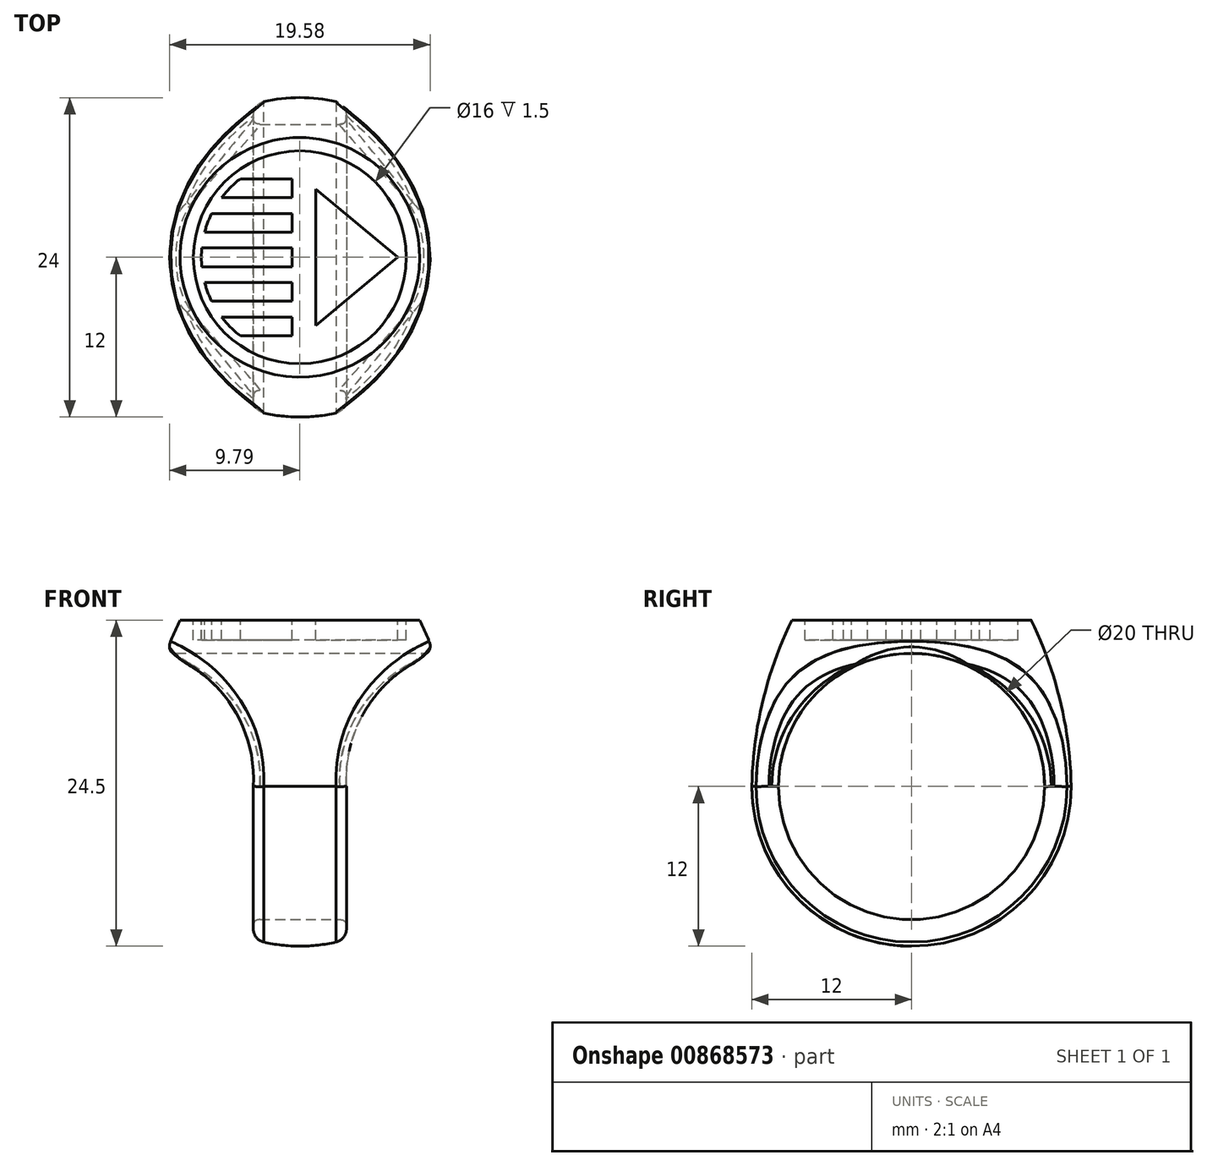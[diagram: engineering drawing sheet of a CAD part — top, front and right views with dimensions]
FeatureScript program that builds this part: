
annotation { "Feature Type Name" : "Feature", "Feature Type Description" : "" }
export const myFeature = defineFeature(function(context is Context, id is Id, definition is map)
    precondition{}
    {
        {
            var Q0;
            Q0=qCreatedBy(makeId("Right.planeOp"),FACE);
            var sketch = newSketch(context, id + "F0", { "sketchPlane" : qUnion([Q0])});
            skLineSegment(sketch, "E0", {"start": v(0, 0) * mm, "end": v(0, -24.5) * mm});
            skLineSegment(sketch, "E1", {"start": v(0, 0) * mm, "end": v(-9, 0) * mm});
            skArc(sketch, "E2", {"start": v(-12, -12.5) * mm, "mid": v(-8.49, -20.99) * mm, "end": v(0, -24.5) * mm});
            skLineSegment(sketch, "E3", {"start": v(0, -12.5) * mm, "end": v(-12, -12.5) * mm, "construction": true});
            skArc(sketch, "E4", {"start": v(-9, 0) * mm, "mid": v(-11.18, -6.09) * mm, "end": v(-12, -12.5) * mm});
            skSolve(sketch);
        }
        {
            var Q0;
            Q0=makeQuery(id+"F0.imprint","IMPRINT",FACE,{"disambiguationData":[TD([[makeQuery(id+"F0.imprint","IMPRINT",EDGE,{"derivedFrom":sQuery(id+"F0.wireOp",EDGE,"E0")}),-1.0]])]});
            var Q1;
            Q1=sQuery(id+"F0.wireOp",EDGE,"E0");
            revolve(context, id + "F1", {"entities" : qUnion([Q0]), "axis" : qUnion([Q1]), "revolveType" : RevolveType.FULL});
        }
        {
            var Q0;
            Q0=qCreatedBy(makeId("Right.planeOp"),FACE);
            var sketch = newSketch(context, id + "F2", { "sketchPlane" : qUnion([Q0])});
            skCircle(sketch, "E5", {"center": v(0, -12.5) * mm, "radius": 10 * mm});
            skSolve(sketch);
        }
        {
            var Q0;
            Q0=qSketchRegion(id+"F2",true);
            extrude(context, id + "F3", {"entities" : qUnion([Q0]), "operationType" : NewBodyOperationType.REMOVE, "endBound" : BoundingType.SYMMETRIC, "oppositeDirection" : true, "depth" : 25 * mm, "offsetDistance" : 25 * mm});
        }
        {
            var Q0;
            Q0=qCreatedBy(makeId("Front.planeOp"),FACE);
            var sketch = newSketch(context, id + "F4", { "sketchPlane" : qUnion([Q0])});
            skLineSegment(sketch, "E6", {"start": v(3.5, -26.5) * mm, "end": v(3.5, -12.5) * mm});
            skArc(sketch, "E7", {"start": v(10.15, -2.5) * mm, "mid": v(5.16, -6.39) * mm, "end": v(3.5, -12.5) * mm});
            skLineSegment(sketch, "E8", {"start": v(10.15, -2.5) * mm, "end": v(11.65, -2.5) * mm});
            skLineSegment(sketch, "E9", {"start": v(11.65, -2.5) * mm, "end": v(11.65, -26.5) * mm});
            skLineSegment(sketch, "E10", {"start": v(11.65, -26.5) * mm, "end": v(3.5, -26.5) * mm});
            skPoint(sketch, "E11.start.orphan", {"position": v(0, -24.5) * mm});
            skLineSegment(sketch, "E12", {"start": v(0, 0) * mm, "end": v(0, -24.5) * mm, "construction": true});
            skLineSegment(sketch, "E13.MirrorCS", {"start": v(-3.5, -26.5) * mm, "end": v(-3.5, -12.5) * mm});
            skArc(sketch, "E14.MirrorCS", {"start": v(-10.15, -2.5) * mm, "mid": v(-5.16, -6.39) * mm, "end": v(-3.5, -12.5) * mm});
            skLineSegment(sketch, "E15.MirrorCS", {"start": v(-11.65, -2.5) * mm, "end": v(-11.65, -26.5) * mm});
            skLineSegment(sketch, "E16.MirrorCS", {"start": v(-11.65, -26.5) * mm, "end": v(-3.5, -26.5) * mm});
            skLineSegment(sketch, "E17.MirrorCS", {"start": v(-10.15, -2.5) * mm, "end": v(-11.65, -2.5) * mm});
            skSolve(sketch);
        }
        {
            var Q0;
            Q0=qSketchRegion(id+"F4",true);
            extrude(context, id + "F5", {"entities" : qUnion([Q0]), "operationType" : NewBodyOperationType.REMOVE, "endBound" : BoundingType.SYMMETRIC, "depth" : 25 * mm, "offsetDistance" : 25 * mm});
        }
        {
            var Q0;
            Q0=makeQuery(id+"F1.opRevolve","SWEPT_FACE",FACE,{"disambiguationData":[OSD([sQuery(id+"F0.wireOp",EDGE,"E1")])]});
            var sketch = newSketch(context, id + "F6", { "sketchPlane" : qUnion([Q0])});
            skCircle(sketch, "E18", {"center": v(0, 0) * mm, "radius": 8 * mm});
            skLineSegment(sketch, "E19", {"start": v(-8, 0) * mm, "end": v(8, 0) * mm, "construction": true});
            skLineSegment(sketch, "E20", {"start": v(0, 7.69) * mm, "end": v(7.93, 1.07) * mm});
            skLineSegment(sketch, "E21", {"start": v(1.2, 0) * mm, "end": v(1.2, 5.13) * mm});
            skLineSegment(sketch, "E22", {"start": v(1.2, 5.13) * mm, "end": v(7.34, 0) * mm});
            skLineSegment(sketch, "E23", {"start": v(0, 7.69) * mm, "end": v(0, 0) * mm});
            skArc(sketch, "E24.trimOffspring", {"start": v(-4.47, 5.9) * mm, "mid": v(-5.22, 5.25) * mm, "end": v(-5.88, 4.5) * mm});
            skLineSegment(sketch, "E25", {"start": v(-7.37, 0.7) * mm, "end": v(-0.6, 0.7) * mm});
            skLineSegment(sketch, "E26", {"start": v(-0.6, 0.7) * mm, "end": v(-0.6, 0) * mm});
            skLineSegment(sketch, "E27", {"start": v(-7.15, 1.9) * mm, "end": v(-0.6, 1.9) * mm});
            skLineSegment(sketch, "E28", {"start": v(-0.6, 1.9) * mm, "end": v(-0.6, 3.3) * mm});
            skLineSegment(sketch, "E29", {"start": v(-0.6, 3.3) * mm, "end": v(-6.62, 3.3) * mm});
            skLineSegment(sketch, "E30", {"start": v(-5.88, 4.5) * mm, "end": v(-0.6, 4.5) * mm});
            skLineSegment(sketch, "E31", {"start": v(-0.6, 4.5) * mm, "end": v(-0.6, 5.9) * mm});
            skLineSegment(sketch, "E32", {"start": v(-0.6, 5.9) * mm, "end": v(-4.47, 5.9) * mm});
            skArc(sketch, "E33.trimOffspring", {"start": v(-7.37, 0.7) * mm, "mid": v(-7.4, 0.35) * mm, "end": v(-7.4, 0) * mm});
            skArc(sketch, "E34.trimOffspring", {"start": v(-6.62, 3.3) * mm, "mid": v(-6.92, 2.61) * mm, "end": v(-7.15, 1.9) * mm});
            skPoint(sketch, "E35.orphan", {"position": v(-0.6, 7.38) * mm});
            skLineSegment(sketch, "E36.MirrorCS", {"start": v(1.2, -5.13) * mm, "end": v(7.34, 0) * mm});
            skLineSegment(sketch, "E37.MirrorCS", {"start": v(0, -7.69) * mm, "end": v(7.93, -1.07) * mm});
            skLineSegment(sketch, "E38.MirrorCS", {"start": v(1.2, 0) * mm, "end": v(1.2, -5.13) * mm});
            skLineSegment(sketch, "E39.MirrorCS", {"start": v(0, -7.69) * mm, "end": v(0, 0) * mm});
            skLineSegment(sketch, "E40.MirrorCS", {"start": v(-5.88, -4.5) * mm, "end": v(-0.6, -4.5) * mm});
            skLineSegment(sketch, "E41.MirrorCS", {"start": v(-0.6, -5.9) * mm, "end": v(-4.47, -5.9) * mm});
            skArc(sketch, "E42.MirrorCS", {"start": v(-4.47, -5.9) * mm, "mid": v(-5.22, -5.25) * mm, "end": v(-5.88, -4.5) * mm});
            skLineSegment(sketch, "E43.MirrorCS", {"start": v(-0.6, -3.3) * mm, "end": v(-6.62, -3.3) * mm});
            skLineSegment(sketch, "E44.MirrorCS", {"start": v(-7.15, -1.9) * mm, "end": v(-0.6, -1.9) * mm});
            skArc(sketch, "E45.MirrorCS", {"start": v(-6.62, -3.3) * mm, "mid": v(-6.92, -2.61) * mm, "end": v(-7.15, -1.9) * mm});
            skLineSegment(sketch, "E46.MirrorCS", {"start": v(-7.37, -0.7) * mm, "end": v(-0.6, -0.7) * mm});
            skArc(sketch, "E47.MirrorCS", {"start": v(-7.37, -0.7) * mm, "mid": v(-7.4, -0.35) * mm, "end": v(-7.4, 0) * mm});
            skLineSegment(sketch, "E48", {"start": v(-0.6, -5.9) * mm, "end": v(-0.6, -4.5) * mm});
            skLineSegment(sketch, "E49", {"start": v(-0.6, -3.3) * mm, "end": v(-0.6, -1.9) * mm});
            skLineSegment(sketch, "E50", {"start": v(-0.6, -0.7) * mm, "end": v(-0.6, 0) * mm});
            skSolve(sketch);
        }
        {
            var Q0;
            Q0=qSketchRegion(id+"F6",true);
            var Q1;
            Q1=makeQuery(id+"F6.imprint","IMPRINT",FACE,{"disambiguationData":[TD([[makeQuery(id+"F6.imprint","IMPRINT",EDGE,{"derivedFrom":sQuery(id+"F6.wireOp",EDGE,"g20j87Mm-wGr7-AMiz-bI8b-qS7GuHKO57cL")}),1.0]])]});
            extrude(context, id + "F7", {"entities" : qUnion([Q0, Q1]), "operationType" : NewBodyOperationType.REMOVE, "oppositeDirection" : true, "depth" : 1.5 * mm, "offsetDistance" : 25 * mm});
        }
        {
            var Q0;
            Q0=makeQuery(id+"F5.boolean.opBoolean","INTERSECT",EDGE,{"disambiguationData":[OD(1.0)],"derivedFrom":[makeQuery(id+"F1.opRevolve","SWEPT_FACE",FACE,{"disambiguationData":[OSD([sQuery(id+"F0.wireOp",EDGE,"E4")])]}),makeQuery(id+"F5.opExtrude","SWEPT_FACE",FACE,{"disambiguationData":[OSD([sQuery(id+"F4.wireOp",EDGE,"E14.MirrorCS")])]})]});
            var Q1;
            Q1=makeQuery(id+"F5.boolean.opBoolean","INTERSECT",EDGE,{"derivedFrom":[makeQuery(id+"F1.opRevolve","SWEPT_FACE",FACE,{"disambiguationData":[OSD([sQuery(id+"F0.wireOp",EDGE,"E2")])]}),makeQuery(id+"F5.opExtrude","SWEPT_FACE",FACE,{"disambiguationData":[OSD([sQuery(id+"F4.wireOp",EDGE,"E13.MirrorCS")])]})]});
            var Q2;
            Q2=makeQuery(id+"F5.boolean.opBoolean","INTERSECT",EDGE,{"disambiguationData":[OD(1.0)],"derivedFrom":[makeQuery(id+"F1.opRevolve","SWEPT_FACE",FACE,{"disambiguationData":[OSD([sQuery(id+"F0.wireOp",EDGE,"E4")])]}),makeQuery(id+"F5.opExtrude","SWEPT_FACE",FACE,{"disambiguationData":[OSD([sQuery(id+"F4.wireOp",EDGE,"E7")])]})]});
            var Q3;
            Q3=makeQuery(id+"F5.boolean.opBoolean","INTERSECT",EDGE,{"derivedFrom":[makeQuery(id+"F1.opRevolve","SWEPT_FACE",FACE,{"disambiguationData":[OSD([sQuery(id+"F0.wireOp",EDGE,"E2")])]}),makeQuery(id+"F5.opExtrude","SWEPT_FACE",FACE,{"disambiguationData":[OSD([sQuery(id+"F4.wireOp",EDGE,"E6")])]})]});
            fillet(context, id + "F8", {"entities" : qUnion([Q0, Q1, Q2, Q3]), "radius" : 1 * mm, "allowEdgeOverflow" : false});
        }
        {
            var Q0;
            Q0=makeQuery(id+"F5.boolean.opBoolean","INTERSECT",EDGE,{"disambiguationData":[OD(1.0)],"derivedFrom":[makeQuery(id+"F3.boolean.opBoolean","COPY",FACE,{"derivedFrom":makeQuery(id+"F3.opExtrude","SWEPT_FACE",FACE,{"disambiguationData":[OSD([sQuery(id+"F2.wireOp",EDGE,"E5")])]})}),makeQuery(id+"F5.opExtrude","SWEPT_FACE",FACE,{"disambiguationData":[OSD([sQuery(id+"F4.wireOp",EDGE,"E14.MirrorCS")])]})]});
            var Q1;
            Q1=makeQuery(id+"F5.boolean.opBoolean","INTERSECT",EDGE,{"derivedFrom":[makeQuery(id+"F3.boolean.opBoolean","COPY",FACE,{"derivedFrom":makeQuery(id+"F3.opExtrude","SWEPT_FACE",FACE,{"disambiguationData":[OSD([sQuery(id+"F2.wireOp",EDGE,"E5")])]})}),makeQuery(id+"F5.opExtrude","SWEPT_FACE",FACE,{"disambiguationData":[OSD([sQuery(id+"F4.wireOp",EDGE,"E13.MirrorCS")])]})]});
            var Q2;
            Q2=makeQuery(id+"F5.boolean.opBoolean","INTERSECT",EDGE,{"disambiguationData":[OD(0.0)],"derivedFrom":[makeQuery(id+"F3.boolean.opBoolean","COPY",FACE,{"derivedFrom":makeQuery(id+"F3.opExtrude","SWEPT_FACE",FACE,{"disambiguationData":[OSD([sQuery(id+"F2.wireOp",EDGE,"E5")])]})}),makeQuery(id+"F5.opExtrude","SWEPT_FACE",FACE,{"disambiguationData":[OSD([sQuery(id+"F4.wireOp",EDGE,"E14.MirrorCS")])]})]});
            var Q3;
            Q3=makeQuery(id+"F5.boolean.opBoolean","INTERSECT",EDGE,{"disambiguationData":[OD(0.0)],"derivedFrom":[makeQuery(id+"F3.boolean.opBoolean","COPY",FACE,{"derivedFrom":makeQuery(id+"F3.opExtrude","SWEPT_FACE",FACE,{"disambiguationData":[OSD([sQuery(id+"F2.wireOp",EDGE,"E5")])]})}),makeQuery(id+"F5.opExtrude","SWEPT_FACE",FACE,{"disambiguationData":[OSD([sQuery(id+"F4.wireOp",EDGE,"E7")])]})]});
            var Q4;
            Q4=makeQuery(id+"F3.boolean.opBoolean","COPY",FACE,{"derivedFrom":makeQuery(id+"F3.opExtrude","SWEPT_FACE",FACE,{"disambiguationData":[OSD([sQuery(id+"F2.wireOp",EDGE,"E5")])]})});
            fillet(context, id + "F9", {"entities" : qUnion([Q0, Q1, Q2, Q3, Q4]), "radius" : .5 * mm, "rho" : 0.5, "crossSection" : FilletCrossSection.CONIC, "allowEdgeOverflow" : false});
        }
    });
